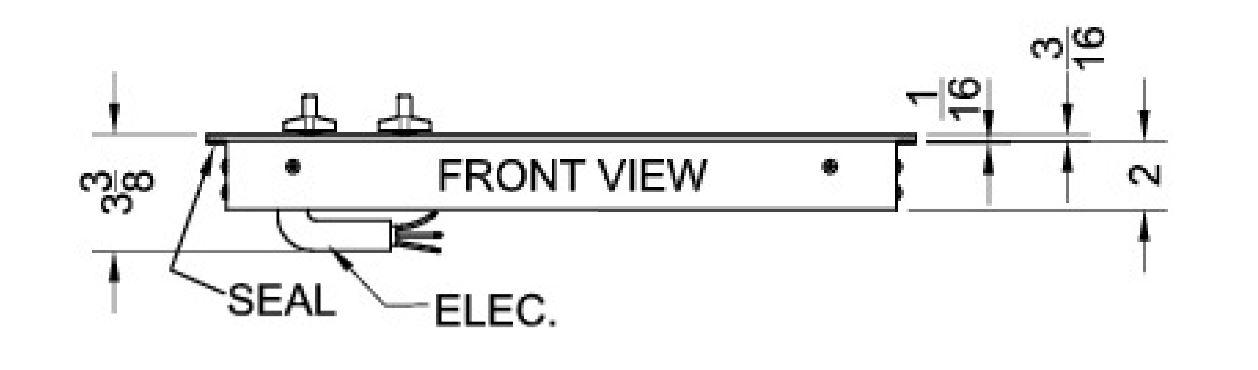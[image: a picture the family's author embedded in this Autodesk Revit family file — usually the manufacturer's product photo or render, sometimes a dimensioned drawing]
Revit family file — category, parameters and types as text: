
# Revit family: QF_Summit_CR5B273B_Electric Cooktop
name_source: partatom
category: Specialty Equipment
units: mm (PartAtom-declared; Revit-internal decimal feet)

## family parameters
Always vertical = Yes
Cut with Voids When Loaded = No
Part Type = Normal
Room Calculation Point = No
Round Connector Dimension = Use Diameter
Shared = No
Work Plane-Based = No

## types (1)
- QF_Summit_CR5B273B_Electric Cooktop
    Apparent Power = 5750 VA
    Conn Conduit = Yes
    Cycle = 60 Hz
    Default Elevation = 0"
    Depth = 20 1/2"
    Description = Electric Cooktop
    Elec Conn Connection Height = 0"
    Elec Conn RI Height = 0"
    FL Amps = 25 A
    Foodservice Equipment Identifier = Yes
    Height = 3 1/8"
    Identify Quantity as Lot = Yes
    Length = 27"
    Manufacturer = Summit
    Max Overcurrent Protection = 0 A
    Min Ckt Ampacity = 0 A
    Model = CR5B273B
    Number of Poles = 1
    Phase = 1
    Volts = 230 V
    Watts = 5750 W
    Weight in Pounds = 35

## geometry (parser evidence)
native form markers: Sweep x1
no freeform markers — native parametric forms only
